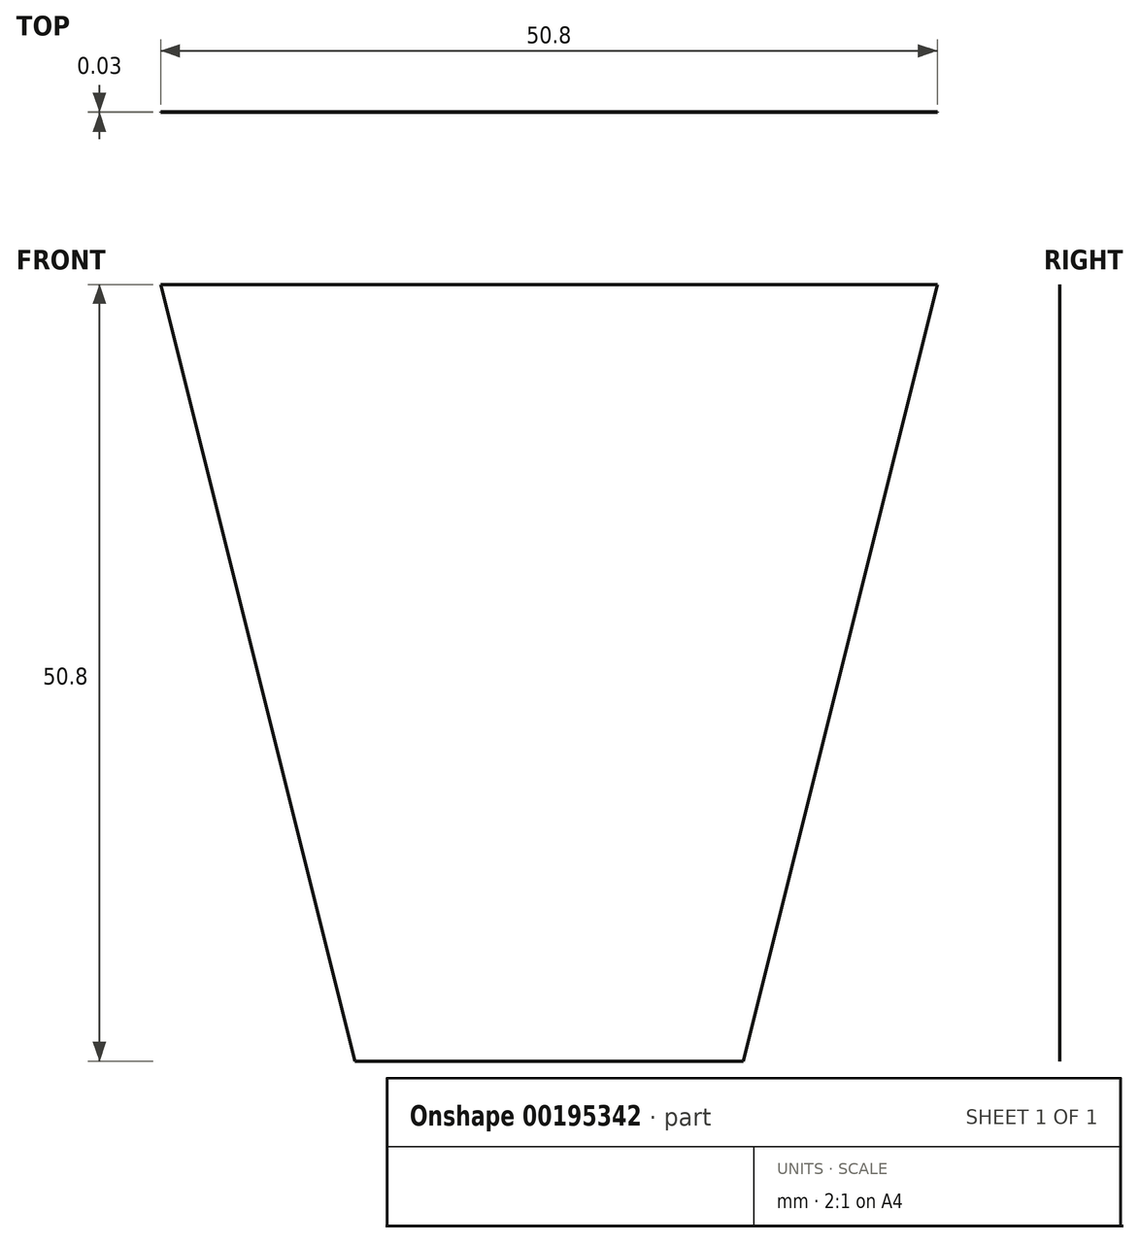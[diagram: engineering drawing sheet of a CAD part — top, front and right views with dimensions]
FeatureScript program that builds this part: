
annotation { "Feature Type Name" : "Feature", "Feature Type Description" : "" }
export const myFeature = defineFeature(function(context is Context, id is Id, definition is map)
    precondition{}
    {
        {
            var Q0;
            Q0=qCreatedBy(makeId("Front.planeOp"),FACE);
            var sketch = newSketch(context, id + "F0", { "sketchPlane" : qUnion([Q0])});
            skLineSegment(sketch, "E0", {"start": v(-25.4, 0) * mm, "end": v(25.4, 0) * mm});
            skLineSegment(sketch, "E1", {"start": v(-25.4, 0) * mm, "end": v(-12.7, -50.8) * mm});
            skLineSegment(sketch, "E2", {"start": v(-12.7, -50.8) * mm, "end": v(12.7, -50.8) * mm});
            skLineSegment(sketch, "E3", {"start": v(12.7, -50.8) * mm, "end": v(25.4, 0) * mm});
            skSolve(sketch);
        }
        {
            var Q0;
            Q0 = qSketchRegion(id + "F0", true);
            extrude(context, id + "F1", {"entities" : qUnion([Q0]), "depth" : 0.03 * mm});
        }
    });
